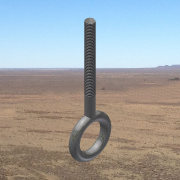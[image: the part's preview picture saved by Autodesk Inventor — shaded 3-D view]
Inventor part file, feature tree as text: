
AUTODESK INVENTOR PART (.ipt)
format: ipt  version: 2013 SP2 (Build 170200200, 200)  size: 161,792 bytes
history: native  units: in
note: dims shown in document units (in); Inventor stores cm internally (conversion verified against a paired STEP export)
features: sketch x3, plane x2, extrude x1, thread x1, revolve x1
ambient origin geometry x8: Origin, YZ Plane, XZ Plane, XY Plane, X Axis, Y Axis, Z Axis, Center Point
bodies: Solid1 (feature_tree)
feature tree (8):
  extrude  "Extrusion1"  Depth=4.0in TaperAngle=0.0deg
  thread  "Thread4"  [1 undecoded]
  sketch  "Sketch2"  dims[d15=-0.1875in d17=0.375in]
  plane  "Work Plane1"
  plane  "Work Plane2"
  revolve  "Revolution1"  [1 undecoded]
  sketch  "Sketch1"  dims[d0=0.375in d2=4.0in d3=0.0in d10=3.0in d11=0.0in]
  sketch  "Sketch5"  dims[d18=0.75in d19=90.0deg]
note: 2 required parameter values undecoded (feature->parameter linkage not recoverable at this tier; creation-order binding heuristic only, values carry confidence <= 0.55)